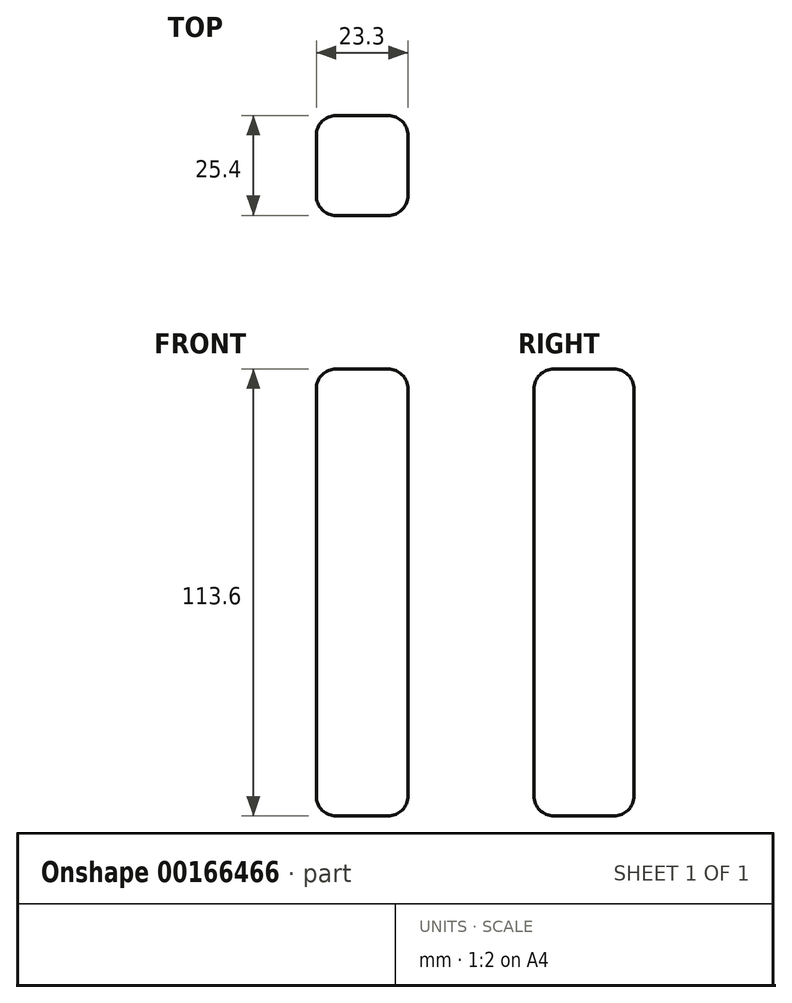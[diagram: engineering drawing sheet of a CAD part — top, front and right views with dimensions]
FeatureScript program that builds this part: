
annotation { "Feature Type Name" : "Feature", "Feature Type Description" : "" }
export const myFeature = defineFeature(function(context is Context, id is Id, definition is map)
    precondition{}
    {
        {
            var Q0;
            Q0=qCreatedBy(makeId("Front.planeOp"),FACE);
            var sketch = newSketch(context, id + "F0", { "sketchPlane" : qUnion([Q0])});
            skLineSegment(sketch, "E0.bottom", {"start": v(-11.65, 55.33) * mm, "end": v(11.65, 55.33) * mm});
            skLineSegment(sketch, "E0.top", {"start": v(-11.65, -58.27) * mm, "end": v(11.65, -58.27) * mm});
            skLineSegment(sketch, "E0.left", {"start": v(-11.65, 55.33) * mm, "end": v(-11.65, -58.27) * mm});
            skLineSegment(sketch, "E0.right", {"start": v(11.65, 55.33) * mm, "end": v(11.65, -58.27) * mm});
            skPoint(sketch, "E0.middle", {"position": v(0, -1.47) * mm});
            skSolve(sketch);
        }
        {
            var Q0;
            Q0 = qSketchRegion(id + "F0", true);
            extrude(context, id + "F1", {"entities" : qUnion([Q0]), "depth" : 25.4 * mm});
        }
        {
            var Q0;
            Q0=makeQuery(id+"F1.opExtrude","CAP_FACE",FACE,{"disambiguationData":[OSD([sQuery(id+"F0.wireOp",EDGE,"E0.bottom"),sQuery(id+"F0.wireOp",EDGE,"E0.top"),sQuery(id+"F0.wireOp",EDGE,"E0.left"),sQuery(id+"F0.wireOp",EDGE,"E0.right")])],"isStart":false});
            fillet(context, id + "F2", {"entities" : qUnion([Q0]), "radius" : 5.08 * mm, "tangentPropagation" : true, "allowEdgeOverflow" : false});
        }
        {
            var Q0;
            Q0=makeQuery(id+"F1.opExtrude","SWEPT_FACE",FACE,{"disambiguationData":[OSD([sQuery(id+"F0.wireOp",EDGE,"E0.right")])]});
            fillet(context, id + "F3", {"entities" : qUnion([Q0]), "radius" : 5.08 * mm, "tangentPropagation" : true, "allowEdgeOverflow" : false});
        }
        {
            var Q0;
            Q0=makeQuery(id+"F1.opExtrude","SWEPT_FACE",FACE,{"disambiguationData":[OSD([sQuery(id+"F0.wireOp",EDGE,"E0.left")])]});
            fillet(context, id + "F4", {"entities" : qUnion([Q0]), "radius" : 5.08 * mm, "tangentPropagation" : true, "allowEdgeOverflow" : false});
        }
        {
            var Q0;
            Q0=makeQuery(id+"F1.opExtrude","CAP_FACE",FACE,{"disambiguationData":[OSD([sQuery(id+"F0.wireOp",EDGE,"E0.bottom"),sQuery(id+"F0.wireOp",EDGE,"E0.top"),sQuery(id+"F0.wireOp",EDGE,"E0.left"),sQuery(id+"F0.wireOp",EDGE,"E0.right")])],"isStart":true});
            fillet(context, id + "F5", {"entities" : qUnion([Q0]), "radius" : 5.08 * mm, "tangentPropagation" : true, "allowEdgeOverflow" : false});
        }
    });
